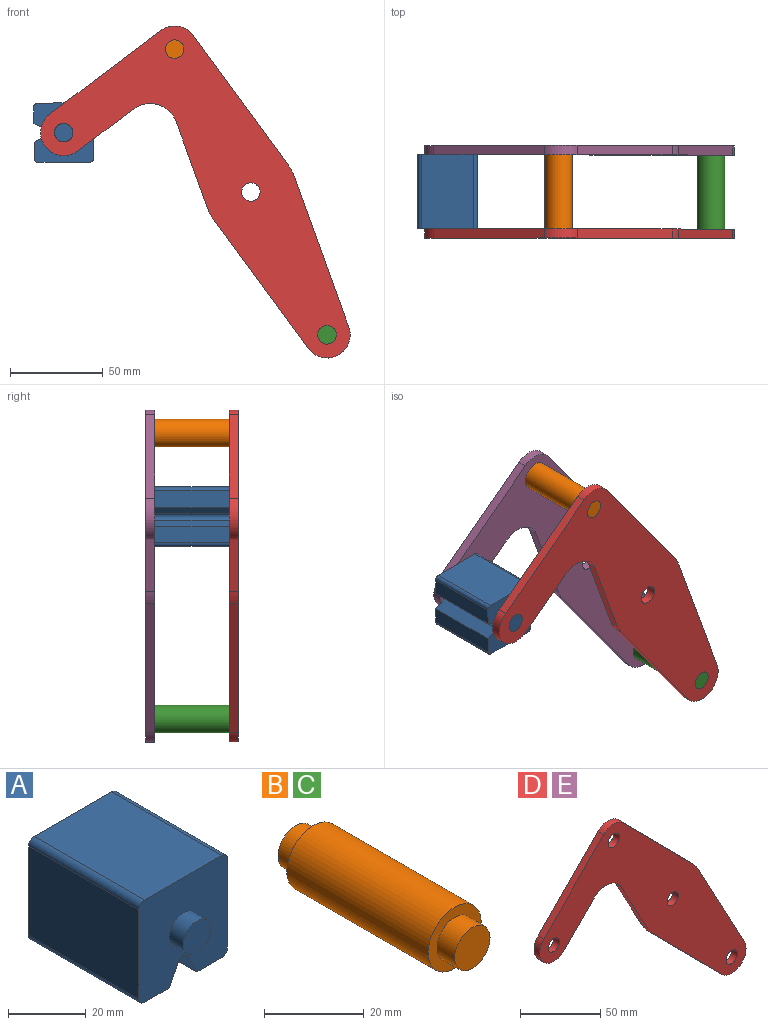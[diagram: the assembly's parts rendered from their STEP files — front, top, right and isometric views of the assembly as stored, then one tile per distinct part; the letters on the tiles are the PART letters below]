
ASSEMBLY  parts=5 mates=3
PART A: 18 faces, bbox 32.1x50x32.1 mm
  f0: plane 40x28.08mm, normal (1,0,0), area 1123.1mm2, adj f4,f10,f13,f14
  f1: plane 40x9.04mm, normal (0,0,-1), area 361.6mm2, adj f2,f4,f10,f14
  f2: plane 40x6.42mm, normal (-0.89,0,-0.45), area 287.2mm2, adj f1,f4,f10,f15
  f3: plane 40x6.42mm, normal (0.89,0,-0.45), area 287.2mm2, adj f4,f5,f10,f15
  f4: plane 32.08x32.08mm, normal (0,-1,0), area 900.6mm2, adj f0,f1,f2,f3,f5,f6,f7,f9
  f5: plane 40x9.04mm, normal (0,0,-1), area 361.6mm2, adj f3,f4,f10,f16
  f6: plane 40x28.08mm, normal (0,0,1), area 1123.1mm2, adj f4,f10,f13,f17
  f7: plane 40x28.08mm, normal (-1,0,0), area 1123.1mm2, adj f4,f10,f16,f17
  f8: plane 10x10mm, normal (0,-1,0), area 78.5mm2, adj f9
  f9: cylinder r=5mm len=10mm, axis (0,1,0), area 157.1mm2, adj f4,f8
  f10: plane 32.08x32.08mm, normal (0,1,0), area 900.6mm2, adj f0,f1,f2,f3,f5,f6,f7,f12
  f11: plane 10x10mm, normal (0,1,0), area 78.5mm2, adj f12
  f12: cylinder r=5mm len=10mm, axis (0,-1,0), area 157.1mm2, adj f10,f11
  f13: cylinder r=2mm len=40mm, axis (0,1,0), area 125.7mm2, adj f0,f4,f6,f10
  f14: cylinder r=2mm len=40mm, axis (0,-1,0), area 125.7mm2, adj f0,f1,f4,f10
  f15: cylinder r=2mm len=40mm, axis (0,1,0), area 177.1mm2, adj f2,f3,f4,f10
  f16: cylinder r=2mm len=40mm, axis (0,1,0), area 125.7mm2, adj f4,f5,f7,f10
  f17: cylinder r=2mm len=40mm, axis (0,-1,0), area 125.7mm2, adj f4,f6,f7,f10
PART B: 7 faces, bbox 15x50x15 mm
  f0: cylinder r=7.5mm len=40mm, axis (0,-1,0), area 1885mm2, adj f2,f5
  f1: cylinder r=5mm len=10mm, axis (0,1,0), area 157.1mm2, adj f2,f3
  f2: plane 15x15mm, normal (0,-1,0), area 98.2mm2, adj f0,f1
  f3: plane 10x10mm, normal (0,-1,0), area 78.5mm2, adj f1
  f4: cylinder r=5mm len=10mm, axis (0,-1,0), area 157.1mm2, adj f5,f6
  f5: plane 15x15mm, normal (0,1,0), area 98.2mm2, adj f0,f4
  f6: plane 10x10mm, normal (0,1,0), area 78.5mm2, adj f4
PART C: same geometry as B
PART D: 18 faces, bbox 181.7x5x165.8 mm
  f0: plane 43.49x23.35mm, normal (-0.88,0,-0.47), area 246.8mm2, adj f1,f14,f16,f17
  f1: cylinder r=25mm len=5.75mm, axis (0,1,0), area 35.8mm2, adj f0,f2,f16,f17
  f2: plane 61.6x60.87mm, normal (-0.71,0,-0.7), area 433mm2, adj f1,f3,f16,f17
  f3: cylinder r=12.5mm len=21.39mm, axis (0,1,0), area 178.4mm2, adj f2,f4,f16,f17
  f4: plane 76.3x40.96mm, normal (0.88,0,0.47), area 433mm2, adj f3,f5,f16,f17
  f5: cylinder r=25mm len=5.75mm, axis (0,1,0), area 35.8mm2, adj f4,f6,f16,f17
  f6: plane 61.6x60.87mm, normal (0.71,0,0.7), area 433mm2, adj f5,f7,f16,f17
  f7: cylinder r=12.5mm len=17.78mm, axis (0,1,0), area 98.9mm2, adj f6,f8,f16,f17
  f8: plane 53.35x52.71mm, normal (-0.71,0,0.7), area 375mm2, adj f7,f9,f16,f17
  f9: cylinder r=12.5mm len=21.39mm, axis (0,1,0), area 196.3mm2, adj f8,f10,f16,f17
  f10: plane 26.86x26.54mm, normal (0.71,0,-0.7), area 188.8mm2, adj f9,f14,f16,f17
  f11: cylinder r=5mm len=10mm, axis (0,1,0), area 157.1mm2, adj f16,f17
  f12: cylinder r=5mm len=10mm, axis (0,1,0), area 157.1mm2, adj f16,f17
  f13: cylinder r=5mm len=10mm, axis (0,1,0), area 157.1mm2, adj f16,f17
  f14: cylinder r=15mm len=23.89mm, axis (0,1,0), area 140.2mm2, adj f0,f10,f16,f17
  f15: cylinder r=5mm len=10mm, axis (0,1,0), area 157.1mm2, adj f16,f17
  f16: plane 181.66x165.78mm, normal (0,-1,0), area 8710.1mm2, adj f0,f1,f2,f3,f4,f5,f6,f7
  f17: plane 181.66x165.78mm, normal (0,1,0), area 8710.1mm2, adj f0,f1,f2,f3,f4,f5,f6,f7
PART E: same geometry as D
PLACE A rot(axis=(0,1,0),89.7deg) t=(-117.51,-20,-72.7)mm
PLACE B rot(axis=(0,1,0),8.4deg) t=(0,-20,0)mm
PLACE C rot(axis=(0,1,0),8.4deg) t=(82.37,-20,-154.4)mm
PLACE D rot(axis=(0,1,0),8.4deg) t=(0,-20,0)mm fixed
PLACE E rot(axis=(0,1,0),8.4deg) t=(0,25,0)mm
MATE fastened C.f0 <-> E.f3  axis (0,1,0) through (41.18,20,-77.2)mm
MATE fastened B.f0 <-> E.f7  axis (0,1,0) through (-41.18,20,77.2)mm
MATE revolute D.f9 <-> A.f9  axis (0,1,0) through (-101.1,-20,32.09)mm
